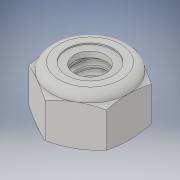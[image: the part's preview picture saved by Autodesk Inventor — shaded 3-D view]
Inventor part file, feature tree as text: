
AUTODESK INVENTOR PART (.ipt)
format: ipt  version: 2018 (Build 220112000, 112)  size: 281,600 bytes
history: native  units: in
note: dims shown in document units (in); Inventor stores cm internally (conversion verified against a paired STEP export)
features: other x1, revolve x1
ambient origin geometry x8: Origin, YZ Plane, XZ Plane, XY Plane, X Axis, Y Axis, Z Axis, Center Point
bodies: Solid1 (feature_tree), Solid2 (feature_tree)
feature tree (2):
  other  "Cut-Revolve4"
  revolve  "Revolve2"  [1 undecoded]
note: 1 required parameter value undecoded (feature->parameter linkage not recoverable at this tier; creation-order binding heuristic only, values carry confidence <= 0.55)
